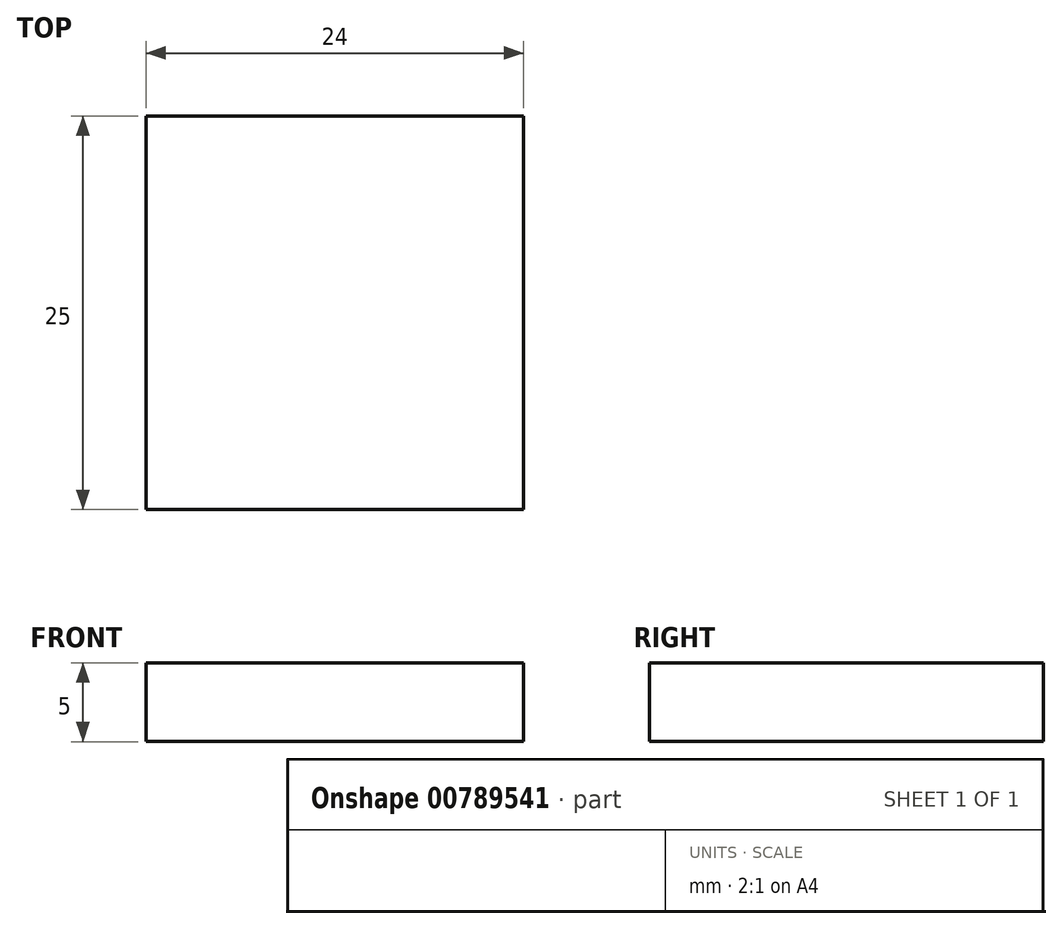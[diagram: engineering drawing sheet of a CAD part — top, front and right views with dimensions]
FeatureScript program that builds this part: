
annotation { "Feature Type Name" : "Feature", "Feature Type Description" : "" }
export const myFeature = defineFeature(function(context is Context, id is Id, definition is map)
    precondition{}
    {
        {
            var Q0;
            Q0=qCreatedBy(makeId("Front.planeOp"),FACE);
            var sketch = newSketch(context, id + "F0", { "sketchPlane" : qUnion([Q0])});
            skLineSegment(sketch, "E0.bottom", {"start": v(11.71, -7.46) * mm, "end": v(-13.29, -7.46) * mm});
            skLineSegment(sketch, "E0.top", {"start": v(11.71, -12.46) * mm, "end": v(-16.29, -12.46) * mm});
            skLineSegment(sketch, "E0.left", {"start": v(11.71, -7.46) * mm, "end": v(11.71, -12.46) * mm});
            skLineSegment(sketch, "E0.right", {"start": v(-12.29, 12.54) * mm, "end": v(-12.29, -12.46) * mm});
            skSolve(sketch);
        }
        {
            var Q0;
            Q0=qSketchRegion(id+"F0",true);
            extrude(context, id + "F1", {"entities" : qUnion([Q0]), "endBound" : BoundingType.SYMMETRIC, "depth" : 25 * mm, "offsetDistance" : 25 * mm});
        }
    });
